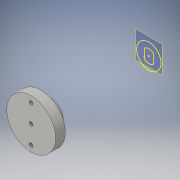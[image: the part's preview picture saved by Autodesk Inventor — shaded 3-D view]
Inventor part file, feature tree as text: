
AUTODESK INVENTOR PART (.ipt)
format: ipt  version: 2016 (Build 200138000, 138)  size: 132,608 bytes
history: native  units: in
note: dims shown in document units (in); Inventor stores cm internally (conversion verified against a paired STEP export)
features: sketch x3, extrude x2, plane x1
ambient origin geometry x8: Origin, YZ Plane, XZ Plane, XY Plane, X Axis, Y Axis, Z Axis, Center Point
bodies: Solid1 (feature_tree)
feature tree (6):
  extrude  "Extrusion1"  Depth=0.2in TaperAngle=0.0deg
  extrude  "Extrusion2"  Depth=0.184in
  plane  "Work Plane1"
  sketch  "Sketch5"  dims[d22=0.266in d23=0.098in d24=0.098in d25=0.5in d26=0.075in d27=1.0in d28=0.075in d29=0.075in]
  sketch  "Sketch1"  dims[d10=0.21in d11=0.0in d16=0.2in d17=0.0in]
  sketch  "Sketch2"  dims[d18=2.0in d21=0.184in]
